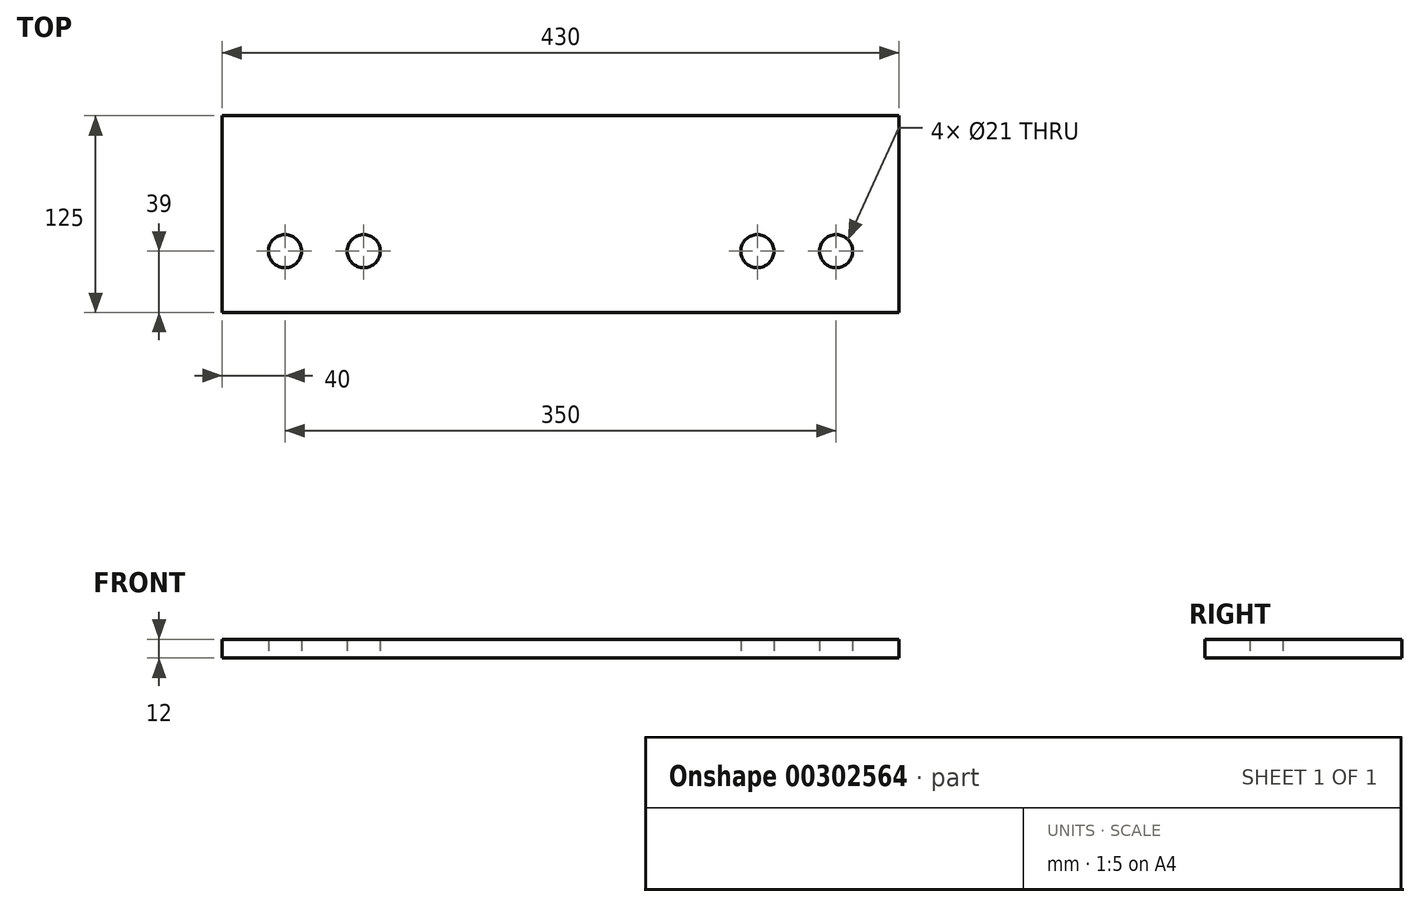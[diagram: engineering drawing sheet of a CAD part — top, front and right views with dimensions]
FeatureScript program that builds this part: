
annotation { "Feature Type Name" : "Feature", "Feature Type Description" : "" }
export const myFeature = defineFeature(function(context is Context, id is Id, definition is map)
    precondition{}
    {
        {
            var Q0;
            Q0=qCreatedBy(makeId("Top.planeOp"),FACE);
            var sketch = newSketch(context, id + "F0", { "sketchPlane" : qUnion([Q0])});
            skLineSegment(sketch, "E0.bottom", {"start": v(0, 0) * mm, "end": v(430, 0) * mm});
            skLineSegment(sketch, "E0.top", {"start": v(0, 125) * mm, "end": v(430, 125) * mm});
            skLineSegment(sketch, "E0.left", {"start": v(0, 0) * mm, "end": v(0, 125) * mm});
            skLineSegment(sketch, "E0.right", {"start": v(430, 0) * mm, "end": v(430, 125) * mm});
            skLineSegment(sketch, "E1", {"start": v(215, 165.6) * mm, "end": v(215, -190.75) * mm});
            skCircle(sketch, "E2", {"center": v(340, 39) * mm, "radius": 10.5 * mm});
            skCircle(sketch, "E3", {"center": v(390, 39) * mm, "radius": 10.5 * mm});
            skCircle(sketch, "E4.MirrorC", {"center": v(90, 39) * mm, "radius": 10.5 * mm});
            skCircle(sketch, "E5.MirrorC", {"center": v(40, 39) * mm, "radius": 10.5 * mm});
            skSolve(sketch);
        }
        {
            var Q0;
            Q0=qSketchRegion(id+"F0",true);
            extrude(context, id + "F1", {"entities" : qUnion([Q0]), "depth" : 12 * mm});
        }
    });
